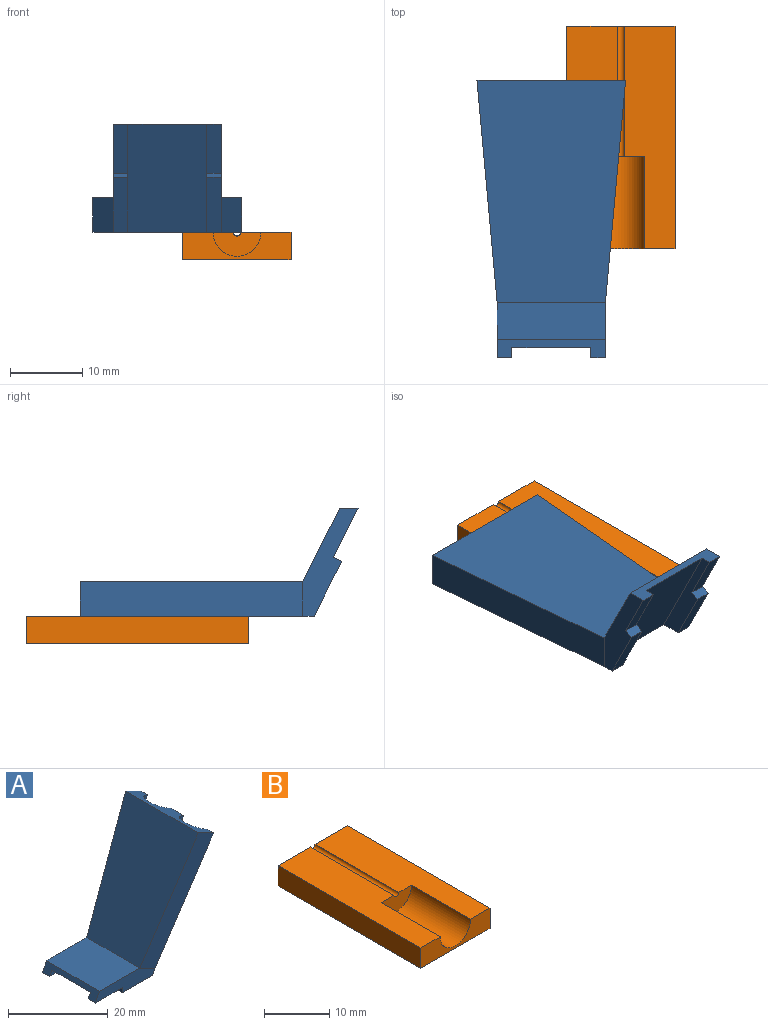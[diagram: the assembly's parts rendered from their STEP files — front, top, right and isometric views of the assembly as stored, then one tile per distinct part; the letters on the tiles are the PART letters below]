
ASSEMBLY  parts=2 mates=1
PART A: 22 faces, bbox 30.6x20.6x31.2 mm
  f0: plane 8.51x2.03mm, normal (0,0,-1), area 17.3mm2, adj f2,f5,f14,f20
  f1: plane 2.03x1.27mm, normal (-1,0,0), area 2.6mm2, adj f7,f8,f13,f19
  f2: plane 29x20.57mm, normal (0.89,0,-0.45), area 372.4mm2, adj f0,f4,f5,f7,f8,f11,f12,f15
  f3: plane 7.62x2.03mm, normal (0,0,-1), area 15.5mm2, adj f5,f6,f14,f20
  f4: plane 20.57x4.32mm, normal (0.45,0,0.89), area 65mm2, adj f2,f9,f11,f12,f15,f17
  f5: plane 16.83x3.56mm, normal (0,-1,0), area 43.7mm2, adj f0,f2,f3,f6,f10,f11,f14
  f6: plane 14.99x2.29mm, normal (-0.89,0,0.45), area 22.8mm2, adj f3,f5,f8,f10,f13,f19,f20,f21
  f7: plane 8.51x2.03mm, normal (0,0,-1), area 17.3mm2, adj f1,f2,f8,f19
  f8: plane 16.83x3.56mm, normal (0,1,0), area 43.7mm2, adj f1,f2,f6,f7,f10,f12,f13
  f9: plane 27.6x20.57mm, normal (-0.89,0,0.45), area 548.7mm2, adj f4,f10,f11,f12
  f10: plane 14.99x11.37mm, normal (0,0,1), area 170.4mm2, adj f5,f6,f8,f9
  f11: plane 29.76x18.11mm, normal (-0.04,-1,-0.08), area 149.5mm2, adj f2,f4,f5,f9
  f12: plane 29.76x18.11mm, normal (-0.04,1,-0.08), area 149.5mm2, adj f2,f4,f8,f9
  f13: plane 7.62x2.03mm, normal (0,0,-1), area 15.5mm2, adj f1,f6,f8,f19
  f14: plane 2.03x1.27mm, normal (-1,0,0), area 2.6mm2, adj f0,f3,f5,f20
  f15: cylinder r=3.3mm len=12.9mm, axis (0.45,0,0.89), area 132.5mm2, adj f2,f4,f16
  f16: plane 6.6x2.95mm, normal (0.45,0,0.89), area 17.1mm2, adj f2,f15
  f17: cylinder r=3.3mm len=12.9mm, axis (0.45,0,0.89), area 132.5mm2, adj f2,f4,f18
  f18: plane 6.6x2.95mm, normal (0.45,0,0.89), area 17.1mm2, adj f2,f17
  f19: plane 17.4x2.54mm, normal (0,-1,0), area 32.5mm2, adj f1,f2,f6,f7,f13,f21
  f20: plane 17.4x2.54mm, normal (0,1,0), area 32.5mm2, adj f0,f2,f3,f6,f14,f21
  f21: plane 16.76x10.92mm, normal (0,0,-1), area 183.1mm2, adj f2,f6,f19,f20
PART B: 10 faces, bbox 15x30.9x3.8 mm
  f0: plane 30.86x6.99mm, normal (0,0,1), area 179.9mm2, adj f2,f5,f6,f7,f8,f9
  f1: plane 30.86x6.99mm, normal (0,0,1), area 179.9mm2, adj f4,f5,f6,f7,f8,f9
  f2: plane 30.86x3.81mm, normal (-1,0,0), area 117.6mm2, adj f0,f3,f5,f6
  f3: plane 30.86x14.99mm, normal (0,0,-1), area 462.5mm2, adj f2,f4,f5,f6
  f4: plane 30.86x3.81mm, normal (1,0,0), area 117.6mm2, adj f1,f3,f5,f6
  f5: plane 14.99x3.81mm, normal (0,-1,0), area 40mm2, adj f0,f1,f2,f3,f4,f7
  f6: plane 14.99x3.81mm, normal (0,1,0), area 56.7mm2, adj f0,f1,f2,f3,f4,f9
  f7: cylinder r=3.3mm len=12.78mm, axis (0,-1,0), area 132.5mm2, adj f0,f1,f5,f8
  f8: plane 6.6x3.3mm, normal (0,-1,0), area 16.7mm2, adj f0,f1,f7,f9
  f9: cylinder r=0.51mm len=18.09mm, axis (0,-1,0), area 28.9mm2, adj f0,f1,f6,f8
PLACE A rot(axis=(-0.47,0.47,0.75),106.1deg) t=(3.22,-9.55,41.32)mm
PLACE B t=(16.87,38.08,26.26)mm
MATE planar A.f2 <-> B.f0  axis (0,0,-1) through (10.71,12.54,25.87)mm
